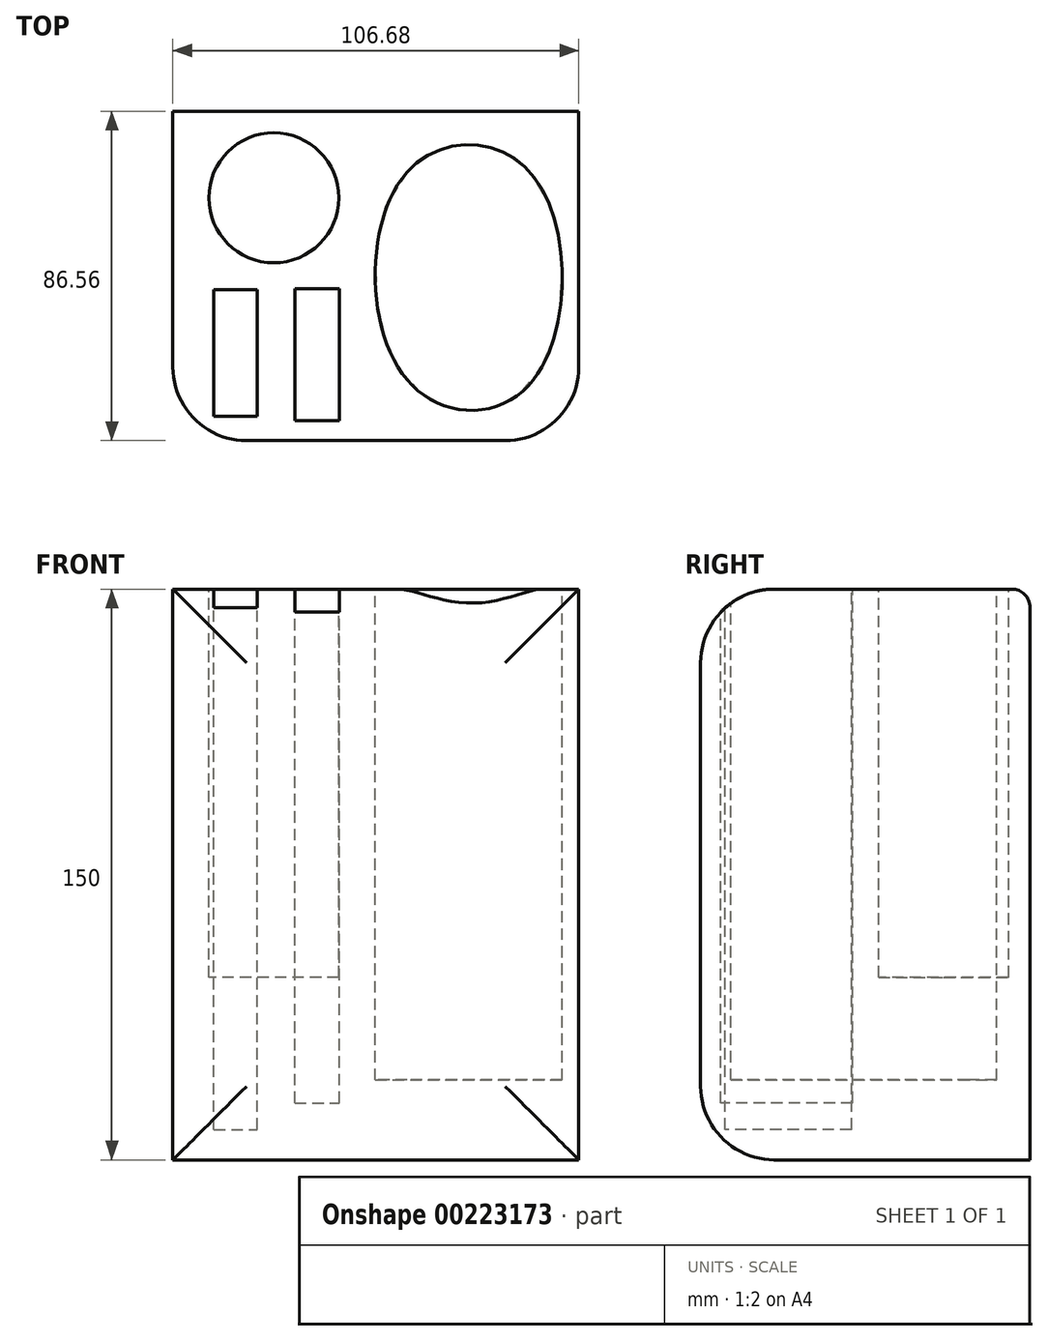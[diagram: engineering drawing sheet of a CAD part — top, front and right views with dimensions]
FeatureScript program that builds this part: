
annotation { "Feature Type Name" : "Feature", "Feature Type Description" : "" }
export const myFeature = defineFeature(function(context is Context, id is Id, definition is map)
    precondition{}
    {
        {
            var Q0;
            Q0=qCreatedBy(makeId("Top.planeOp"),FACE);
            var sketch = newSketch(context, id + "F0", { "sketchPlane" : qUnion([Q0])});
            skLineSegment(sketch, "E0.bottom", {"start": v(-53.34, 43.28) * mm, "end": v(53.34, 43.28) * mm});
            skLineSegment(sketch, "E0.top", {"start": v(-53.34, -43.28) * mm, "end": v(53.34, -43.28) * mm});
            skLineSegment(sketch, "E0.left", {"start": v(-53.34, 43.28) * mm, "end": v(-53.34, -43.28) * mm});
            skLineSegment(sketch, "E0.right", {"start": v(53.34, 43.28) * mm, "end": v(53.34, -43.28) * mm});
            skPoint(sketch, "E0.middle", {"position": v(0, 0) * mm});
            skSolve(sketch);
        }
        {
            var Q0;
            Q0=makeQuery(id+"F0.imprint","IMPRINT",FACE,{"disambiguationData":[TD([[makeQuery(id+"F0.imprint","IMPRINT",EDGE,{"derivedFrom":sQuery(id+"F0.wireOp",EDGE,"E0.bottom")}),-1.0]])]});
            extrude(context, id + "F1", {"entities" : qUnion([Q0]), "depth" : 150 * mm});
        }
        {
            var Q0;
            Q0=makeQuery(id+"F1.opExtrude","CAP_FACE",FACE,{"disambiguationData":[OSD([sQuery(id+"F0.wireOp",EDGE,"E0.bottom"),sQuery(id+"F0.wireOp",EDGE,"E0.top"),sQuery(id+"F0.wireOp",EDGE,"E0.left"),sQuery(id+"F0.wireOp",EDGE,"E0.right")])],"isStart":false});
            var sketch = newSketch(context, id + "F2", { "sketchPlane" : qUnion([Q0])});
            skCircle(sketch, "E1", {"center": v(-26.82, 20.55) * mm, "radius": 17.08 * mm});
            skSolve(sketch);
        }
        {
            var Q0;
            Q0=makeQuery(id+"F2.imprint","IMPRINT",FACE,{"disambiguationData":[TD([[makeQuery(id+"F2.imprint","IMPRINT",EDGE,{"derivedFrom":sQuery(id+"F2.wireOp",EDGE,"E1")}),-1.0]])]});
            var sketch = newSketch(context, id + "F3", { "sketchPlane" : qUnion([Q0])});
            skFitSpline(sketch, "E2", {"points": [v(8.16, 27.25) * mm, v(8.16, -27.25) * mm, v(40.22, -28.71) * mm, v(40.8, 26.96) * mm, v(8.16, 27.25) * mm]});
            skSolve(sketch);
        }
        {
            var Q0;
            Q0=makeQuery(id+"F2.imprint","IMPRINT",FACE,{"disambiguationData":[TD([[makeQuery(id+"F2.imprint","IMPRINT",EDGE,{"derivedFrom":sQuery(id+"F2.wireOp",EDGE,"E1")}),-1.0]])]});
            var sketch = newSketch(context, id + "F4", { "sketchPlane" : qUnion([Q0])});
            skLineSegment(sketch, "E3.bottom", {"start": v(-42.56, -3.64) * mm, "end": v(-31.19, -3.64) * mm});
            skLineSegment(sketch, "E3.top", {"start": v(-42.56, -36.87) * mm, "end": v(-31.19, -36.87) * mm});
            skLineSegment(sketch, "E3.left", {"start": v(-42.56, -3.64) * mm, "end": v(-42.56, -36.87) * mm});
            skLineSegment(sketch, "E3.right", {"start": v(-31.19, -3.64) * mm, "end": v(-31.19, -36.87) * mm});
            skSolve(sketch);
        }
        {
            var Q0;
            Q0=makeQuery(id+"F2.imprint","IMPRINT",FACE,{"disambiguationData":[TD([[makeQuery(id+"F2.imprint","IMPRINT",EDGE,{"derivedFrom":sQuery(id+"F2.wireOp",EDGE,"E1")}),-1.0]])]});
            var sketch = newSketch(context, id + "F5", { "sketchPlane" : qUnion([Q0])});
            skLineSegment(sketch, "E4.bottom", {"start": v(-21.28, -3.35) * mm, "end": v(-9.62, -3.35) * mm});
            skLineSegment(sketch, "E4.top", {"start": v(-21.28, -38.04) * mm, "end": v(-9.62, -38.04) * mm});
            skLineSegment(sketch, "E4.left", {"start": v(-21.28, -3.35) * mm, "end": v(-21.28, -38.04) * mm});
            skLineSegment(sketch, "E4.right", {"start": v(-9.62, -3.35) * mm, "end": v(-9.62, -38.04) * mm});
            skSolve(sketch);
        }
        {
            var Q0;
            Q0=makeQuery(id+"F3.imprint","IMPRINT",FACE,{"disambiguationData":[TD([[makeQuery(id+"F3.imprint","IMPRINT",EDGE,{"derivedFrom":sQuery(id+"F3.wireOp",EDGE,"E2")}),1.0]])]});
            extrude(context, id + "F6", {"entities" : qUnion([Q0]), "operationType" : NewBodyOperationType.REMOVE, "oppositeDirection" : true, "depth" : 129 * mm});
        }
        {
            var Q0;
            Q0=makeQuery(id+"F2.imprint","IMPRINT",FACE,{"disambiguationData":[TD([[makeQuery(id+"F2.imprint","IMPRINT",EDGE,{"derivedFrom":sQuery(id+"F2.wireOp",EDGE,"E1")}),1.0]])]});
            extrude(context, id + "F7", {"entities" : qUnion([Q0]), "operationType" : NewBodyOperationType.REMOVE, "oppositeDirection" : true, "depth" : 102 * mm});
        }
        {
            var Q0;
            Q0=makeQuery(id+"F5.imprint","IMPRINT",FACE,{"disambiguationData":[TD([[makeQuery(id+"F5.imprint","IMPRINT",EDGE,{"derivedFrom":sQuery(id+"F5.wireOp",EDGE,"E4.bottom")}),-1.0]])]});
            extrude(context, id + "F8", {"entities" : qUnion([Q0]), "operationType" : NewBodyOperationType.REMOVE, "oppositeDirection" : true, "depth" : 135 * mm});
        }
        {
            var Q0;
            Q0=makeQuery(id+"F4.imprint","IMPRINT",FACE,{"disambiguationData":[TD([[makeQuery(id+"F4.imprint","IMPRINT",EDGE,{"derivedFrom":sQuery(id+"F4.wireOp",EDGE,"E3.bottom")}),-1.0]])]});
            extrude(context, id + "F9", {"entities" : qUnion([Q0]), "operationType" : NewBodyOperationType.REMOVE, "oppositeDirection" : true, "depth" : 142 * mm});
        }
        {
            var Q0;
            Q0=makeQuery(id+"F1.opExtrude","SWEPT_FACE",FACE,{"disambiguationData":[OSD([sQuery(id+"F0.wireOp",EDGE,"E0.top")])]});
            fillet(context, id + "F10", {"entities" : qUnion([Q0]), "radius" : 19.3 * mm, "tangentPropagation" : true, "allowEdgeOverflow" : false});
        }
        {
            var Q0;
            Q0=makeQuery(id+"F1.opExtrude","CAP_EDGE",EDGE,{"disambiguationData":[OSD([sQuery(id+"F0.wireOp",EDGE,"E0.bottom")])],"isStart":false});
            fillet(context, id + "F11", {"entities" : qUnion([Q0]), "radius" : 4.83 * mm, "tangentPropagation" : true, "allowEdgeOverflow" : false});
        }
    });
